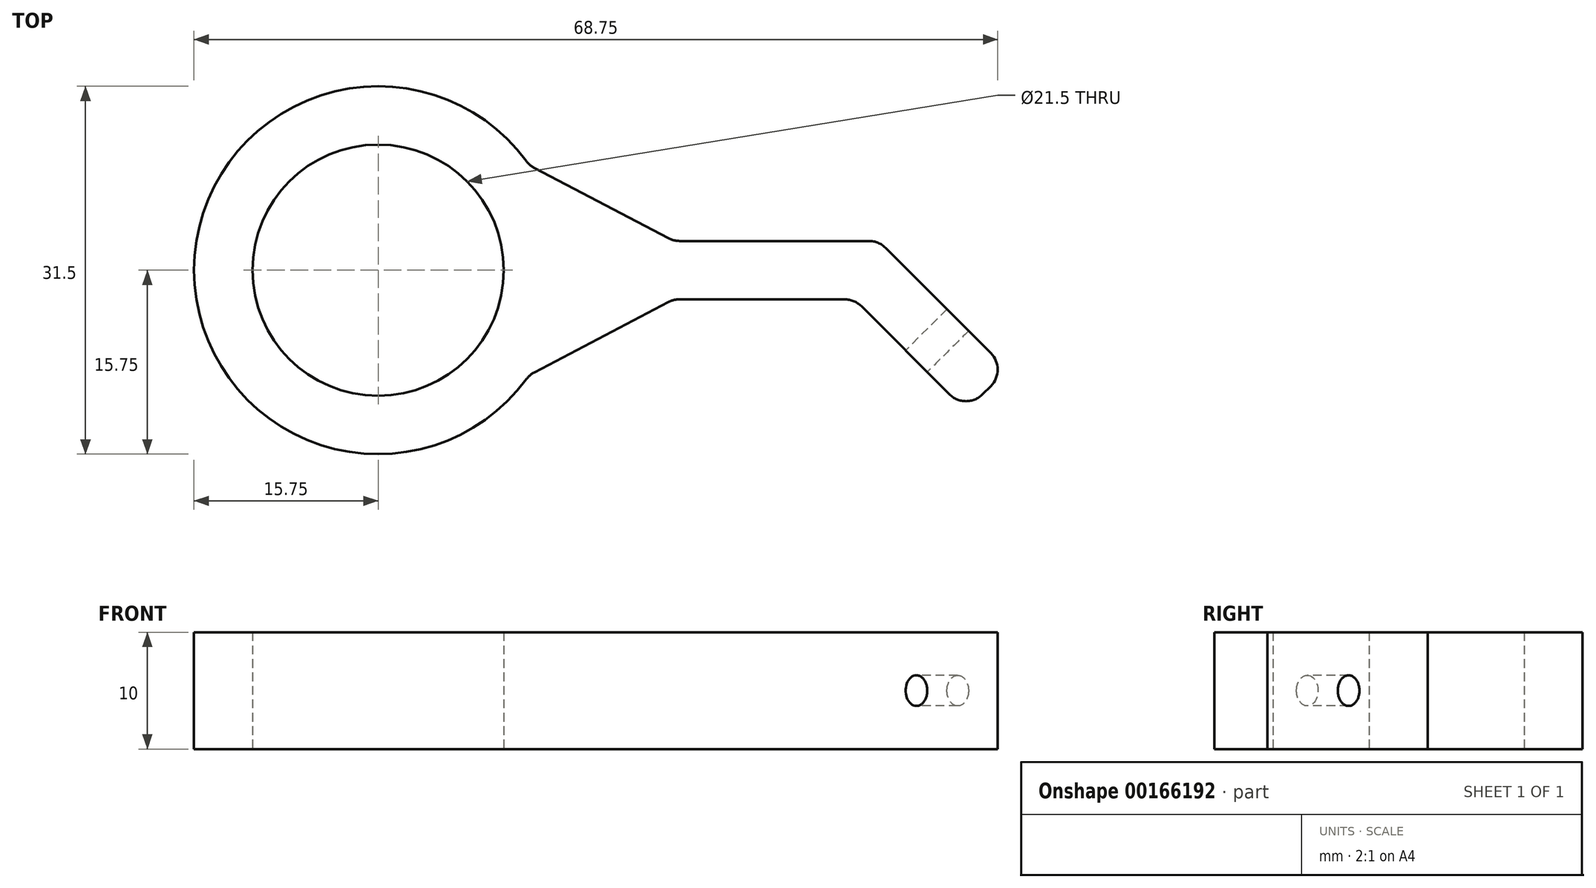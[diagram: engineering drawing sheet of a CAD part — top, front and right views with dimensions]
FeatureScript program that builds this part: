
annotation { "Feature Type Name" : "Feature", "Feature Type Description" : "" }
export const myFeature = defineFeature(function(context is Context, id is Id, definition is map)
    precondition{}
    {
        {
            var Q0;
            Q0=qCreatedBy(makeId("Top.planeOp"),FACE);
            var sketch = newSketch(context, id + "F0", { "sketchPlane" : qUnion([Q0])});
            skCircle(sketch, "E0", {"center": v(0, 0) * mm, "radius": 10.75 * mm});
            skArc(sketch, "E1", {"start": v(15.55, 2.5) * mm, "mid": v(-15.75, 0) * mm, "end": v(15.55, -2.5) * mm});
            skLineSegment(sketch, "E2", {"start": v(15.55, 2.5) * mm, "end": v(40.75, 2.5) * mm});
            skLineSegment(sketch, "E3", {"start": v(53.83, -8.51) * mm, "end": v(50.3, -12.05) * mm});
            skLineSegment(sketch, "E4", {"start": v(50.3, -12.05) * mm, "end": v(40.75, -2.5) * mm});
            skLineSegment(sketch, "E5", {"start": v(40.75, -2.5) * mm, "end": v(15.55, -2.5) * mm});
            skLineSegment(sketch, "E6", {"start": v(40.75, 2.5) * mm, "end": v(40.75, -2.5) * mm, "construction": true});
            skLineSegment(sketch, "E7", {"start": v(40.75, 2.5) * mm, "end": v(42.82, 2.5) * mm});
            skLineSegment(sketch, "E8", {"start": v(42.82, 2.5) * mm, "end": v(53.83, -8.51) * mm});
            skSolve(sketch);
        }
        {
            var Q0;
            Q0 = qSketchRegion(id + "F0", true);
            extrude(context, id + "F1", {"entities" : qUnion([Q0]), "depth" : 10 * mm});
        }
        {
            var Q0;
            Q0=makeQuery(id+"F1.opExtrude","SWEPT_EDGE",EDGE,{"disambiguationData":[OSD([sQuery(id+"F0.wireOp",EDGE,"E1"),sQuery(id+"F0.wireOp",EDGE,"E5")])]});
            var Q1;
            Q1=makeQuery(id+"F1.opExtrude","SWEPT_EDGE",EDGE,{"disambiguationData":[OSD([sQuery(id+"F0.wireOp",EDGE,"E1"),sQuery(id+"F0.wireOp",EDGE,"E2")])]});
            chamfer(context, id + "F2", {"entities" : qUnion([Q0, Q1]), "width" : 15 * mm, "tangentPropagation" : true});
        }
        {
            var Q0;
            Q0=makeQuery(id+"F1.opExtrude","SWEPT_FACE",FACE,{"disambiguationData":[OSD([sQuery(id+"F0.wireOp",EDGE,"E4")])]});
            var sketch = newSketch(context, id + "F3", { "sketchPlane" : qUnion([Q0])});
            skCircle(sketch, "E9", {"center": v(38.08, 5) * mm, "radius": 1.31 * mm});
            skPoint(sketch, "E9.centerSnap0", {"position": v(44.08, 5) * mm});
            skSolve(sketch);
        }
        {
            var Q0;
            Q0 = qSketchRegion(id + "F3", true);
            extrude(context, id + "F4", {"entities" : qUnion([Q0]), "operationType" : NewBodyOperationType.REMOVE, "oppositeDirection" : true, "depth" : 25 * mm});
        }
        {
            var Q0;
            Q0=makeQuery(id+"F1.opExtrude","SWEPT_EDGE",EDGE,{"disambiguationData":[OSD([sQuery(id+"F0.wireOp",EDGE,"E3"),sQuery(id+"F0.wireOp",EDGE,"E4")])]});
            var Q1;
            Q1=makeQuery(id+"F1.opExtrude","SWEPT_EDGE",EDGE,{"disambiguationData":[OSD([sQuery(id+"F0.wireOp",EDGE,"E3"),sQuery(id+"F0.wireOp",EDGE,"E8")])]});
            var Q2;
            Q2=makeQuery(id+"F1.opExtrude","SWEPT_EDGE",EDGE,{"disambiguationData":[OSD([sQuery(id+"F0.wireOp",EDGE,"E4"),sQuery(id+"F0.wireOp",EDGE,"E5")])]});
            var Q3;
            {var subQ0=sQuery(id+"F0.wireOp",EDGE,"E5");Q3=makeQuery(id+"F2.opChamfer","BLEND_EDGE",EDGE,{"blendedFrom":[makeQuery(id+"F1.opExtrude","SWEPT_EDGE",EDGE,{"disambiguationData":[OSD([sQuery(id+"F0.wireOp",EDGE,"E1"),subQ0])]}),makeQuery(id+"F1.opExtrude","SWEPT_FACE",FACE,{"disambiguationData":[OSD([subQ0])]})],"blendedInto":[makeQuery(id+"F1.opExtrude","SWEPT_FACE",FACE,{"disambiguationData":[OSD([subQ0])]})]});}
            var Q4;
            {var subQ0=sQuery(id+"F0.wireOp",EDGE,"E1");Q4=makeQuery(id+"F2.opChamfer","BLEND_EDGE",EDGE,{"blendedFrom":[makeQuery(id+"F1.opExtrude","SWEPT_EDGE",EDGE,{"disambiguationData":[OSD([subQ0,sQuery(id+"F0.wireOp",EDGE,"E5")])]}),makeQuery(id+"F1.opExtrude","SWEPT_FACE",FACE,{"disambiguationData":[OSD([subQ0])]})],"blendedInto":[makeQuery(id+"F1.opExtrude","SWEPT_FACE",FACE,{"disambiguationData":[OSD([subQ0])]})]});}
            var Q5;
            Q5=makeQuery(id+"F1.opExtrude","SWEPT_EDGE",EDGE,{"disambiguationData":[OSD([sQuery(id+"F0.wireOp",EDGE,"E7"),sQuery(id+"F0.wireOp",EDGE,"E8")])]});
            var Q6;
            {var subQ0=sQuery(id+"F0.wireOp",EDGE,"E2");Q6=makeQuery(id+"F2.opChamfer","BLEND_EDGE",EDGE,{"blendedFrom":[makeQuery(id+"F1.opExtrude","SWEPT_EDGE",EDGE,{"disambiguationData":[OSD([sQuery(id+"F0.wireOp",EDGE,"E1"),subQ0])]}),makeQuery(id+"F1.opExtrude","SWEPT_FACE",FACE,{"disambiguationData":[OSD([subQ0,sQuery(id+"F0.wireOp",EDGE,"E7")])]})],"blendedInto":[makeQuery(id+"F1.opExtrude","SWEPT_FACE",FACE,{"disambiguationData":[OSD([subQ0,sQuery(id+"F0.wireOp",EDGE,"E7")])]})]});}
            var Q7;
            {var subQ0=sQuery(id+"F0.wireOp",EDGE,"E1");Q7=makeQuery(id+"F2.opChamfer","BLEND_EDGE",EDGE,{"blendedFrom":[makeQuery(id+"F1.opExtrude","SWEPT_EDGE",EDGE,{"disambiguationData":[OSD([subQ0,sQuery(id+"F0.wireOp",EDGE,"E2")])]}),makeQuery(id+"F1.opExtrude","SWEPT_FACE",FACE,{"disambiguationData":[OSD([subQ0])]})],"blendedInto":[makeQuery(id+"F1.opExtrude","SWEPT_FACE",FACE,{"disambiguationData":[OSD([subQ0])]})]});}
            fillet(context, id + "F5", {"entities" : qUnion([Q0, Q1, Q2, Q3, Q4, Q5, Q6, Q7]), "radius" : 2 * mm, "tangentPropagation" : true, "allowEdgeOverflow" : false});
        }
    });
